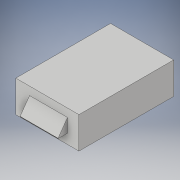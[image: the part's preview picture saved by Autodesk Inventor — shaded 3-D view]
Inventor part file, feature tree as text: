
AUTODESK INVENTOR PART (.ipt)
format: ipt  version: 2019 (Build 230136000, 136)  size: 99,840 bytes
history: native  units: mm
features: extrude x2, sketch x2, chamfer x1
ambient origin geometry x8: Origin, YZ Plane, XZ Plane, XY Plane, X Axis, Y Axis, Z Axis, Center Point
bodies: Solid1 (feature_tree)
feature tree (5):
  extrude  "Extrusion1"  Depth=5.0mm
  extrude  "Extrusion2"  Depth=1.5mm TaperAngle=0.0deg
  chamfer  "Chamfer1"  Distance=1.5mm Angle=45.0deg
  sketch  "Sketch1"  dims[d0=10.0mm d1=5.0mm]
  sketch  "Sketch2"  dims[d2=15.0mm d3=0.0mm d4=1.5mm d5=0.0mm d6=2.1mm d7=1.5mm d8=45.0deg]
